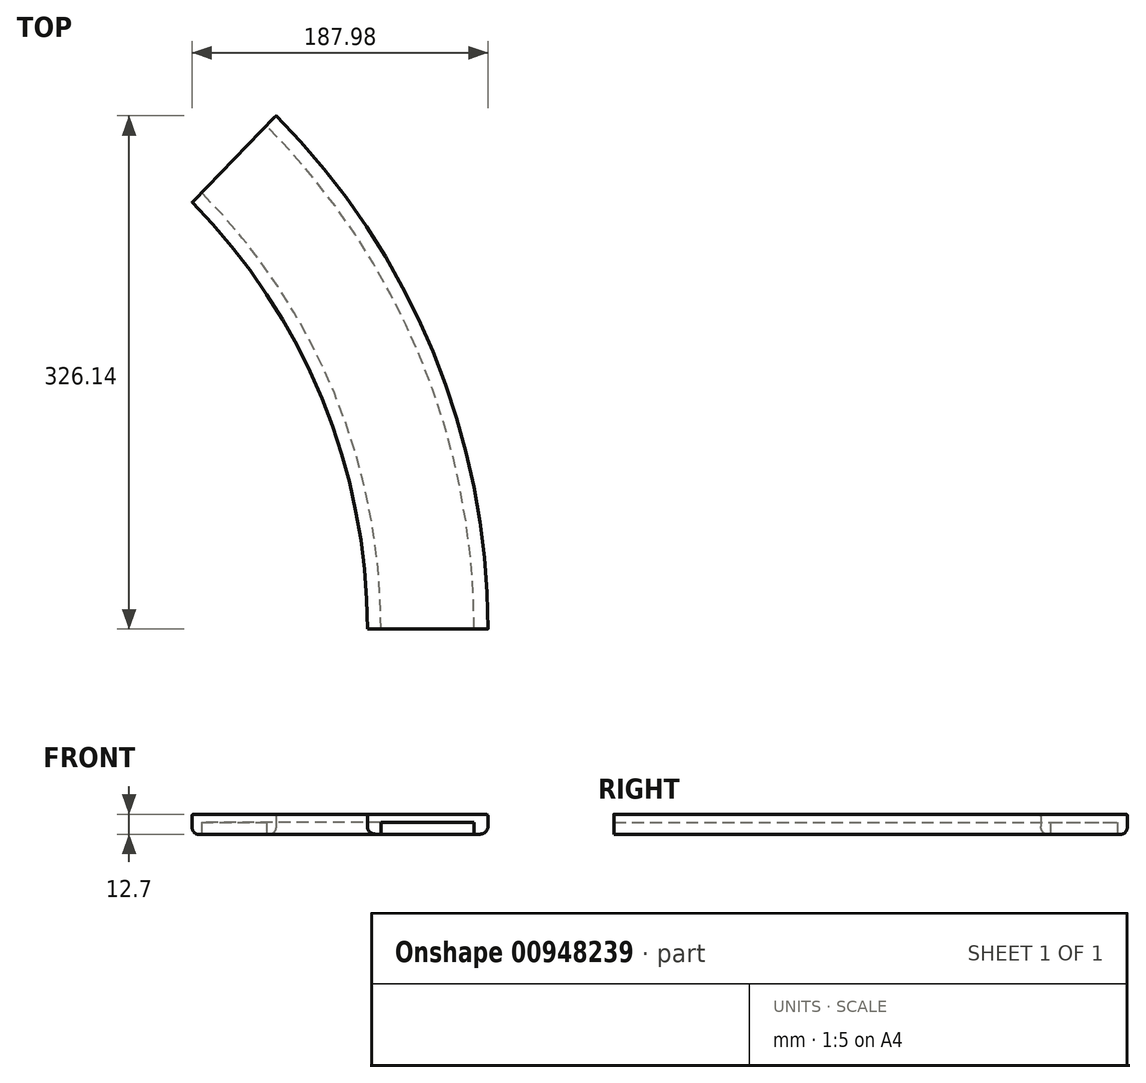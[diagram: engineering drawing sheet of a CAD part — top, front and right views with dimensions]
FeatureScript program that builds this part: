
annotation { "Feature Type Name" : "Feature", "Feature Type Description" : "" }
export const myFeature = defineFeature(function(context is Context, id is Id, definition is map)
    precondition{}
    {
        {
            var Q0;
            Q0=qCreatedBy(makeId("Top.planeOp"),FACE);
            var sketch = newSketch(context, id + "F0", { "sketchPlane" : qUnion([Q0])});
            skCircle(sketch, "E0", {"center": v(0, 0) * mm, "radius": 385.77 * mm});
            skCircle(sketch, "E1", {"center": v(0, 0) * mm, "radius": 462.36 * mm});
            skLineSegment(sketch, "E2", {"start": v(385.77, 0) * mm, "end": v(462.36, 0) * mm});
            skLineSegment(sketch, "E3", {"start": v(0, 0) * mm, "end": v(0, 374.35) * mm});
            skLineSegment(sketch, "E4", {"start": v(0, 374.35) * mm, "end": v(385.77, 0) * mm});
            skLineSegment(sketch, "E5", {"start": v(0, 0) * mm, "end": v(192.88, 187.18) * mm});
            skLineSegment(sketch, "E6", {"start": v(192.88, 187.18) * mm, "end": v(327.74, 326.14) * mm});
            skCircle(sketch, "E7", {"center": v(0, 0) * mm, "radius": 394.4 * mm});
            skCircle(sketch, "E8", {"center": v(0, 0) * mm, "radius": 453.56 * mm});
            skSolve(sketch);
        }
        {
            var Q0;
            {var subQ0=sQuery(id+"F0.wireOp",EDGE,"E2");Q0=makeQuery(id+"F0.imprint","IMPRINT",FACE,{"disambiguationData":[TD([[makeQuery(id+"F0.imprint","IMPRINT",EDGE,{"derivedFrom":subQ0}),1.0]])]});}
            extrude(context, id + "F1", {"entities" : qUnion([Q0]), "depth" : 12.7 * mm, "offsetDistance" : 25.4 * mm});
        }
        {
            var Q0;
            {var subQ0=sQuery(id+"F0.wireOp",EDGE,"E7");var subQ1=sQuery(id+"F0.wireOp",EDGE,"E2");var subQ2=makeQuery(id+"F0.imprint","INTERSECT",VERTEX,{"derivedFrom":[subQ1,subQ0]});Q0=makeQuery(id+"F0.imprint","IMPRINT",FACE,{"disambiguationData":[TD([[makeQuery(id+"F0.imprint","IMPRINT",EDGE,{"disambiguationData":[TD([[subQ2,-1.0]])],"derivedFrom":subQ1}),1.0]])]});}
            var Q1;
            {var subQ0=sQuery(id+"F0.wireOp",EDGE,"E7");var subQ1=sQuery(id+"F0.wireOp",EDGE,"E2");var subQ2=makeQuery(id+"F0.imprint","INTERSECT",VERTEX,{"derivedFrom":[subQ1,subQ0]});Q1=makeQuery(id+"F0.imprint","IMPRINT",FACE,{"disambiguationData":[TD([[makeQuery(id+"F0.imprint","IMPRINT",EDGE,{"disambiguationData":[TD([[subQ2,-1.0]])],"derivedFrom":subQ1}),-1.0]])]});}
            extrude(context, id + "F2", {"entities" : qUnion([Q0, Q1]), "operationType" : NewBodyOperationType.REMOVE, "depth" : 7.62 * mm, "offsetDistance" : 25.4 * mm});
        }
        {
            var Q0;
            Q0=makeQuery(id+"F1.opExtrude","CAP_EDGE",EDGE,{"disambiguationData":[OSD([sQuery(id+"F0.wireOp",EDGE,"E1")])],"isStart":true});
            fillet(context, id + "F3", {"entities" : qUnion([Q0]), "radius" : 5.08 * mm, "tangentPropagation" : true, "allowEdgeOverflow" : false});
        }
        {
            var Q0;
            Q0=makeQuery(id+"F1.opExtrude","CAP_EDGE",EDGE,{"disambiguationData":[OSD([sQuery(id+"F0.wireOp",EDGE,"E0")])],"isStart":true});
            fillet(context, id + "F4", {"entities" : qUnion([Q0]), "radius" : 5.08 * mm, "tangentPropagation" : true, "allowEdgeOverflow" : false});
        }
        {
            var Q0;
            Q0=makeQuery(id+"F1.opExtrude","CAP_EDGE",EDGE,{"disambiguationData":[OSD([sQuery(id+"F0.wireOp",EDGE,"E1")])],"isStart":false});
            fillet(context, id + "F5", {"entities" : qUnion([Q0]), "radius" : 1.27 * mm, "tangentPropagation" : true, "allowEdgeOverflow" : false});
        }
        {
            var Q0;
            Q0=makeQuery(id+"F1.opExtrude","CAP_EDGE",EDGE,{"disambiguationData":[OSD([sQuery(id+"F0.wireOp",EDGE,"E0")])],"isStart":false});
            fillet(context, id + "F6", {"entities" : qUnion([Q0]), "radius" : 1.27 * mm, "tangentPropagation" : true, "allowEdgeOverflow" : false});
        }
    });
